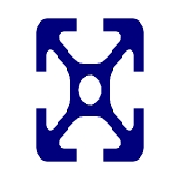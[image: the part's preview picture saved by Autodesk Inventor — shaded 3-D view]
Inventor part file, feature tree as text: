
AUTODESK INVENTOR PART (.ipt)
format: ipt  version: 2020 (Build 240168000, 168)  size: 276,992 bytes
history: native  units: mm
features: other x16, sketch x8, plane x1, split x1
ambient origin geometry x8: Origin, YZ Plane, XZ Plane, XY Plane, X Axis, Y Axis, Z Axis, Center Point
bodies: Body (feature_tree)
feature tree (26):
  other  "Řízená délka"
  other  "Těleso1"
  other  "Start Plane"
  other  "End Plane"
  other  "iFeatureSketch"
  other  "DRAZKA_20:1"
  other  "DRAZKA_20:2"
  other  "DRAZKA_20:3"
  other  "DRAZKA_20:4"
  other  "DIRA_20:1"
  other  "DRAZKA_20:1Axis"
  other  "DRAZKA_20:2Axis"
  other  "DRAZKA_20:3Axis"
  other  "DRAZKA_20:4Axis"
  other  "DIRA_20:1Axis"
  plane  "Work Plane5"
  split  "Split1"
  sketch  "Sketch"  dims[d2=20.0mm d3=20.0mm d4=2.0mm d9=-0.0mm d10=233.481641mm d11=0.13mm d12=0.0mm d15=0.83mm d16=0.83mm d17=9.8mm d18=3.0mm d19=4.55mm d20=45.0deg d21=5.2mm d22=1.8mm d24=1.0mm d26=0.83mm d27=0.83mm d28=9.8mm d29=3.0mm d30=4.55mm d31=45.0deg d32=5.2mm d33=1.8mm d35=1.0mm d37=0.83mm d38=0.83mm d39=9.8mm d40=3.0mm d41=4.55mm d42=45.0deg d43=5.2mm d44=1.8mm d46=1.0mm d48=0.83mm d49=0.83mm d50=9.8mm d51=3.0mm d52=4.55mm d53=45.0deg d54=5.2mm d55=1.8mm d57=1.0mm d59=4.3mm d60=0.0mm d61=0.0mm d62=0.0mm d63=0.0mm d64=0.0mm d65=0.0mm d66=0.0mm d67=0.0mm d76=90.0deg d14=233.481641mm]
  sketch  "Náčrt11"
  other  "Pracovní rovina4"
  sketch  "Náčrt12"
  sketch  "Náčrt6"
  sketch  "Náčrt7"
  sketch  "Náčrt8"
  sketch  "Náčrt9"
  sketch  "Náčrt10"
